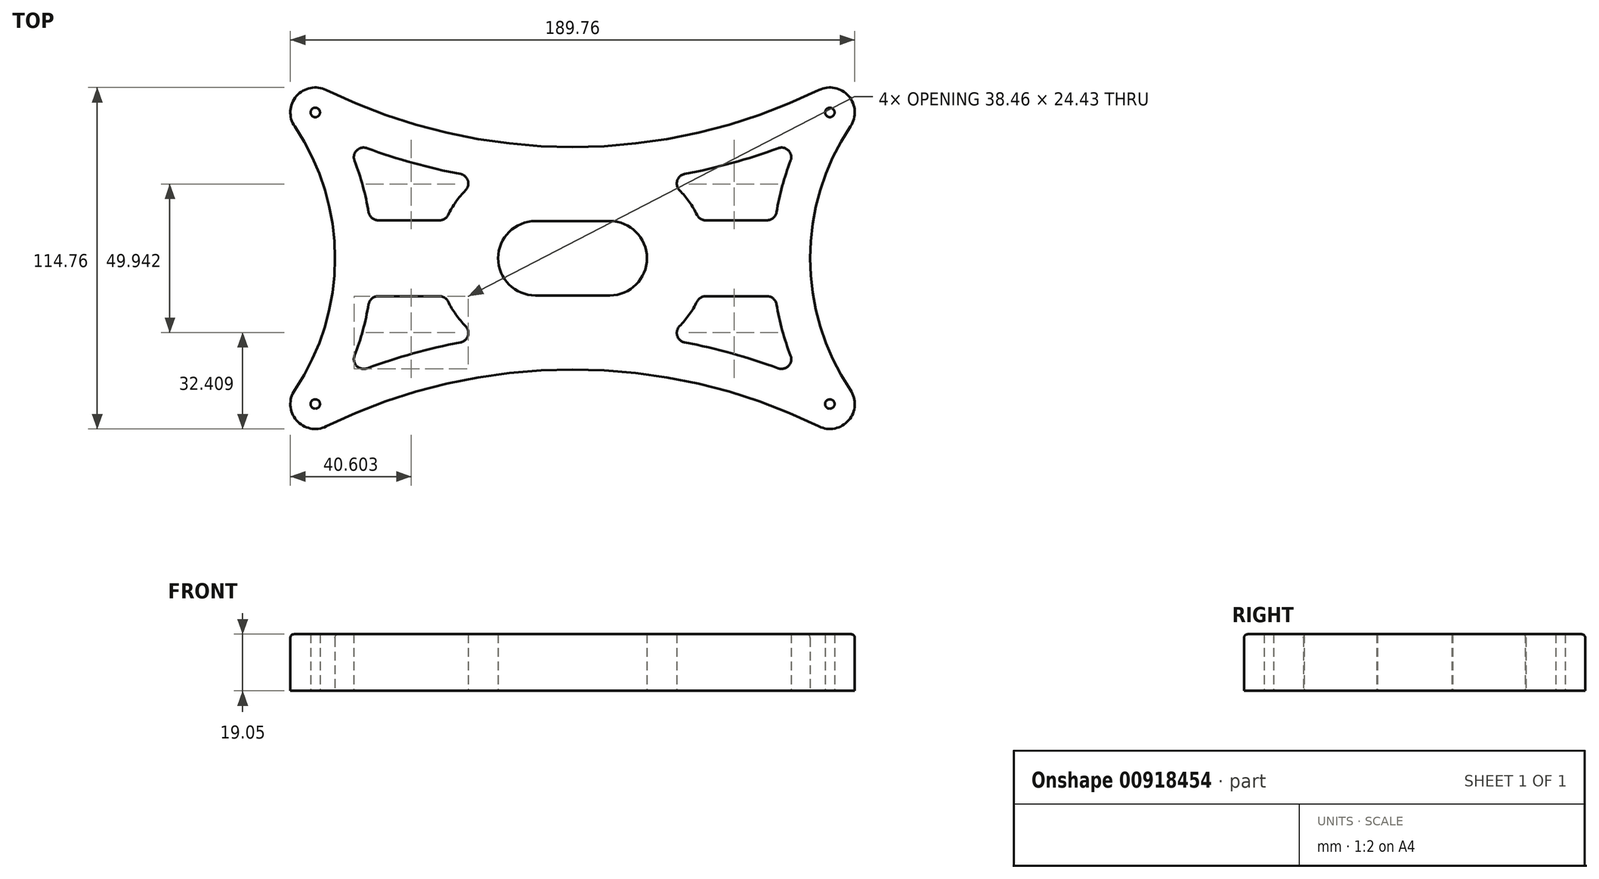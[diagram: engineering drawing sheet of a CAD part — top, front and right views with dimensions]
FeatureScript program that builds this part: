
annotation { "Feature Type Name" : "Feature", "Feature Type Description" : "" }
export const myFeature = defineFeature(function(context is Context, id is Id, definition is map)
    precondition{}
    {
        {
            var Q0;
            Q0=qCreatedBy(makeId("Top.planeOp"),FACE);
            var sketch = newSketch(context, id + "F0", { "sketchPlane" : qUnion([Q0])});
            skLineSegment(sketch, "E0.bottom", {"start": v(-102.5, 65) * mm, "end": v(102.5, 65) * mm, "construction": true});
            skLineSegment(sketch, "E0.top", {"start": v(-102.5, -65) * mm, "end": v(102.5, -65) * mm, "construction": true});
            skLineSegment(sketch, "E0.left", {"start": v(-102.5, 65) * mm, "end": v(-102.5, -65) * mm, "construction": true});
            skLineSegment(sketch, "E0.right", {"start": v(102.5, 65) * mm, "end": v(102.5, -65) * mm, "construction": true});
            skPoint(sketch, "E0.middle", {"position": v(0, 0) * mm});
            skArc(sketch, "E1", {"start": v(-79.48, 63.38) * mm, "mid": v(-98.58, 59.5) * mm, "end": v(-99.76, 40.04) * mm, "construction": true});
            skArc(sketch, "E2.MirrorC", {"start": v(79.48, 63.38) * mm, "mid": v(98.58, 59.5) * mm, "end": v(99.76, 40.04) * mm, "construction": true});
            skArc(sketch, "E3.MirrorC", {"start": v(79.48, -63.38) * mm, "mid": v(98.58, -59.5) * mm, "end": v(99.76, -40.04) * mm, "construction": true});
            skArc(sketch, "E4.MirrorC", {"start": v(-79.48, -63.38) * mm, "mid": v(-98.58, -59.5) * mm, "end": v(-99.76, -40.04) * mm, "construction": true});
            skLineSegment(sketch, "E5", {"start": v(0, 0) * mm, "end": v(0, 365.73) * mm, "construction": true});
            skPoint(sketch, "E5.endSnap0", {"position": v(0, 65) * mm});
            skLineSegment(sketch, "E6", {"start": v(0, 0) * mm, "end": v(0, -420.15) * mm, "construction": true});
            skLineSegment(sketch, "E7", {"start": v(0, 0) * mm, "end": v(397.25, 0) * mm, "construction": true});
            skPoint(sketch, "E7.endSnap0", {"position": v(102.5, 0) * mm});
            skLineSegment(sketch, "E8", {"start": v(0, 0) * mm, "end": v(-430.2, 0) * mm, "construction": true});
            skPoint(sketch, "E9", {"position": v(0, 45) * mm});
            skPoint(sketch, "E10", {"position": v(0, -45) * mm});
            skPoint(sketch, "E11", {"position": v(-87.5, 0) * mm});
            skPoint(sketch, "E12", {"position": v(87.5, 0) * mm});
            skArc(sketch, "E13", {"start": v(-79.48, 63.38) * mm, "mid": v(0, 45) * mm, "end": v(79.48, 63.38) * mm, "construction": true});
            skArc(sketch, "E14.MirrorC", {"start": v(-79.48, -63.38) * mm, "mid": v(0, -45) * mm, "end": v(79.48, -63.38) * mm, "construction": true});
            skArc(sketch, "E15", {"start": v(99.76, 40.04) * mm, "mid": v(87.5, 0) * mm, "end": v(99.76, -40.04) * mm, "construction": true});
            skArc(sketch, "E16.MirrorC", {"start": v(-99.76, 40.04) * mm, "mid": v(-87.5, 0) * mm, "end": v(-99.76, -40.04) * mm, "construction": true});
            skArc(sketch, "E17", {"start": v(-12.5, 12.5) * mm, "mid": v(-25, 0) * mm, "end": v(-12.5, -12.5) * mm});
            skArc(sketch, "E18.MirrorC", {"start": v(12.5, 12.5) * mm, "mid": v(25, 0) * mm, "end": v(12.5, -12.5) * mm});
            skLineSegment(sketch, "E19", {"start": v(-12.5, 12.5) * mm, "end": v(12.5, 12.5) * mm});
            skLineSegment(sketch, "E20", {"start": v(-12.5, -12.5) * mm, "end": v(12.5, -12.5) * mm});
            skArc(sketch, "E21.0", {"start": v(73.54, 32.7) * mm, "mid": v(70.75, 24.17) * mm, "end": v(68.8, 15.41) * mm, "construction": true});
            skArc(sketch, "E21.1", {"start": v(-69.07, 37.24) * mm, "mid": v(-53.53, 32.26) * mm, "end": v(-37.64, 28.55) * mm, "construction": true});
            skArc(sketch, "E21.2", {"start": v(-73.54, 32.7) * mm, "mid": v(-70.75, 24.17) * mm, "end": v(-68.8, 15.41) * mm, "construction": true});
            skArc(sketch, "E21.3", {"start": v(-69.07, -37.24) * mm, "mid": v(-53.53, -32.26) * mm, "end": v(-37.64, -28.55) * mm, "construction": true});
            skArc(sketch, "E22.0", {"start": v(-35.78, 22.67) * mm, "mid": v(-39.02, 18.79) * mm, "end": v(-41.61, 14.44) * mm, "construction": true});
            skArc(sketch, "E22.2", {"start": v(35.78, 22.67) * mm, "mid": v(39.02, 18.79) * mm, "end": v(41.61, 14.44) * mm, "construction": true});
            skPoint(sketch, "E23.visualSharp", {"position": v(-76.83, 40.26) * mm});
            skArc(sketch, "E23.filletArc", {"start": v(-69.07, 37.24) * mm, "mid": v(-72.76, 36.4) * mm, "end": v(-73.54, 32.7) * mm, "construction": true});
            skLineSegment(sketch, "E24", {"start": v(-44.75, 12.5) * mm, "end": v(-65.36, 12.5) * mm, "construction": true});
            skLineSegment(sketch, "E25", {"start": v(-44.75, -12.5) * mm, "end": v(-65.36, -12.5) * mm, "construction": true});
            skLineSegment(sketch, "E26", {"start": v(44.75, 12.5) * mm, "end": v(65.36, 12.5) * mm, "construction": true});
            skLineSegment(sketch, "E27", {"start": v(44.75, -12.5) * mm, "end": v(65.36, -12.5) * mm, "construction": true});
            skArc(sketch, "E28.trimOffspring", {"start": v(41.61, -14.44) * mm, "mid": v(39.02, -18.79) * mm, "end": v(35.78, -22.67) * mm, "construction": true});
            skArc(sketch, "E29.trimOffspring", {"start": v(68.8, -15.41) * mm, "mid": v(70.75, -24.17) * mm, "end": v(73.54, -32.7) * mm, "construction": true});
            skArc(sketch, "E30.trimOffspring", {"start": v(37.64, 28.55) * mm, "mid": v(53.53, 32.26) * mm, "end": v(69.07, 37.24) * mm, "construction": true});
            skArc(sketch, "E31.trimOffspring", {"start": v(37.64, -28.55) * mm, "mid": v(53.53, -32.26) * mm, "end": v(69.07, -37.24) * mm, "construction": true});
            skArc(sketch, "E32.trimOffspring", {"start": v(-41.61, -14.44) * mm, "mid": v(-39.02, -18.79) * mm, "end": v(-35.78, -22.67) * mm, "construction": true});
            skArc(sketch, "E33.trimOffspring", {"start": v(-68.8, -15.41) * mm, "mid": v(-70.75, -24.17) * mm, "end": v(-73.54, -32.7) * mm, "construction": true});
            skPoint(sketch, "E34.visualSharp", {"position": v(-30.17, 27.28) * mm});
            skArc(sketch, "E34.filletArc", {"start": v(-35.78, 22.67) * mm, "mid": v(-34.95, 26.17) * mm, "end": v(-37.64, 28.55) * mm, "construction": true});
            skPoint(sketch, "E35.visualSharp", {"position": v(-42.5, 12.5) * mm});
            skArc(sketch, "E35.filletArc", {"start": v(-44.75, 12.5) * mm, "mid": v(-42.9, 13.03) * mm, "end": v(-41.61, 14.44) * mm, "construction": true});
            skPoint(sketch, "E36.visualSharp", {"position": v(-68.36, 12.5) * mm});
            skArc(sketch, "E36.filletArc", {"start": v(-68.8, 15.41) * mm, "mid": v(-67.61, 13.32) * mm, "end": v(-65.36, 12.5) * mm, "construction": true});
            skPoint(sketch, "E37.visualSharp", {"position": v(-68.36, -12.5) * mm});
            skArc(sketch, "E37.filletArc", {"start": v(-65.36, -12.5) * mm, "mid": v(-67.61, -13.32) * mm, "end": v(-68.8, -15.41) * mm, "construction": true});
            skPoint(sketch, "E38.visualSharp", {"position": v(-42.5, -12.5) * mm});
            skArc(sketch, "E38.filletArc", {"start": v(-41.61, -14.44) * mm, "mid": v(-42.9, -13.03) * mm, "end": v(-44.75, -12.5) * mm, "construction": true});
            skPoint(sketch, "E39.visualSharp", {"position": v(-30.17, -27.28) * mm});
            skArc(sketch, "E39.filletArc", {"start": v(-37.64, -28.55) * mm, "mid": v(-34.95, -26.17) * mm, "end": v(-35.78, -22.67) * mm, "construction": true});
            skPoint(sketch, "E40.visualSharp", {"position": v(-76.83, -40.26) * mm});
            skArc(sketch, "E40.filletArc", {"start": v(-73.54, -32.7) * mm, "mid": v(-72.76, -36.4) * mm, "end": v(-69.07, -37.24) * mm, "construction": true});
            skPoint(sketch, "E41.visualSharp", {"position": v(30.17, 27.28) * mm});
            skArc(sketch, "E41.filletArc", {"start": v(37.64, 28.55) * mm, "mid": v(34.95, 26.17) * mm, "end": v(35.78, 22.67) * mm, "construction": true});
            skPoint(sketch, "E42.visualSharp", {"position": v(76.83, 40.26) * mm});
            skArc(sketch, "E42.filletArc", {"start": v(73.54, 32.7) * mm, "mid": v(72.76, 36.4) * mm, "end": v(69.07, 37.24) * mm, "construction": true});
            skPoint(sketch, "E43.visualSharp", {"position": v(68.36, 12.5) * mm});
            skArc(sketch, "E43.filletArc", {"start": v(65.36, 12.5) * mm, "mid": v(67.61, 13.32) * mm, "end": v(68.8, 15.41) * mm, "construction": true});
            skPoint(sketch, "E44.visualSharp", {"position": v(42.5, 12.5) * mm});
            skArc(sketch, "E44.filletArc", {"start": v(41.61, 14.44) * mm, "mid": v(42.9, 13.03) * mm, "end": v(44.75, 12.5) * mm, "construction": true});
            skPoint(sketch, "E45.visualSharp", {"position": v(42.5, -12.5) * mm});
            skArc(sketch, "E45.filletArc", {"start": v(44.75, -12.5) * mm, "mid": v(42.9, -13.03) * mm, "end": v(41.61, -14.44) * mm, "construction": true});
            skPoint(sketch, "E46.visualSharp", {"position": v(68.36, -12.5) * mm});
            skArc(sketch, "E46.filletArc", {"start": v(68.8, -15.41) * mm, "mid": v(67.61, -13.32) * mm, "end": v(65.36, -12.5) * mm, "construction": true});
            skPoint(sketch, "E47.visualSharp", {"position": v(76.83, -40.26) * mm});
            skArc(sketch, "E47.filletArc", {"start": v(69.07, -37.24) * mm, "mid": v(72.76, -36.4) * mm, "end": v(73.54, -32.7) * mm, "construction": true});
            skPoint(sketch, "E48.visualSharp", {"position": v(30.17, -27.28) * mm});
            skArc(sketch, "E48.filletArc", {"start": v(35.78, -22.67) * mm, "mid": v(34.95, -26.17) * mm, "end": v(37.64, -28.55) * mm, "construction": true});
            skCircle(sketch, "E49", {"center": v(-12.5, 0) * mm, "radius": 3.18 * mm});
            skCircle(sketch, "E50", {"center": v(12.5, 0) * mm, "radius": 3.18 * mm});
            skArc(sketch, "E51.0", {"start": v(-82.82, 56.53) * mm, "mid": v(-92.82, 54.5) * mm, "end": v(-93.44, 44.3) * mm});
            skArc(sketch, "E51.1", {"start": v(-93.44, 44.3) * mm, "mid": v(-79.88, 0) * mm, "end": v(-93.44, -44.3) * mm});
            skArc(sketch, "E51.2", {"start": v(-82.82, 56.53) * mm, "mid": v(0, 37.38) * mm, "end": v(82.82, 56.53) * mm});
            skArc(sketch, "E51.3", {"start": v(-82.82, -56.53) * mm, "mid": v(-92.82, -54.5) * mm, "end": v(-93.44, -44.3) * mm});
            skArc(sketch, "E51.4", {"start": v(82.82, 56.53) * mm, "mid": v(92.82, 54.5) * mm, "end": v(93.44, 44.3) * mm});
            skArc(sketch, "E51.5", {"start": v(93.44, 44.3) * mm, "mid": v(79.88, 0) * mm, "end": v(93.44, -44.3) * mm});
            skArc(sketch, "E51.6", {"start": v(82.82, -56.53) * mm, "mid": v(92.82, -54.5) * mm, "end": v(93.44, -44.3) * mm});
            skArc(sketch, "E51.7", {"start": v(-82.82, -56.53) * mm, "mid": v(0, -37.38) * mm, "end": v(82.82, -56.53) * mm});
            skCircle(sketch, "E52", {"center": v(-86.5, -49) * mm, "radius": 1.59 * mm});
            skCircle(sketch, "E53", {"center": v(86.5, -49) * mm, "radius": 1.59 * mm});
            skCircle(sketch, "E54", {"center": v(86.5, 49) * mm, "radius": 1.59 * mm});
            skCircle(sketch, "E55", {"center": v(-86.5, 49) * mm, "radius": 1.59 * mm});
            skArc(sketch, "E56.0", {"start": v(-41.84, -14.56) * mm, "mid": v(-43.04, -13.24) * mm, "end": v(-44.75, -12.75) * mm});
            skArc(sketch, "E56.1", {"start": v(-41.84, -14.56) * mm, "mid": v(-39.23, -18.93) * mm, "end": v(-35.97, -22.85) * mm});
            skLineSegment(sketch, "E56.2", {"start": v(-44.75, -12.75) * mm, "end": v(-65.36, -12.75) * mm});
            skArc(sketch, "E56.3", {"start": v(-37.68, -28.3) * mm, "mid": v(-35.2, -26.1) * mm, "end": v(-35.97, -22.85) * mm});
            skArc(sketch, "E56.4", {"start": v(-65.36, -12.75) * mm, "mid": v(-67.45, -13.52) * mm, "end": v(-68.56, -15.45) * mm});
            skArc(sketch, "E56.5", {"start": v(-68.56, -15.45) * mm, "mid": v(-70.5, -24.24) * mm, "end": v(-73.3, -32.79) * mm});
            skArc(sketch, "E56.6", {"start": v(-73.3, -32.79) * mm, "mid": v(-72.58, -36.23) * mm, "end": v(-69.16, -37) * mm});
            skArc(sketch, "E56.7", {"start": v(-69.16, -37) * mm, "mid": v(-53.6, -32.01) * mm, "end": v(-37.68, -28.3) * mm});
            skLineSegment(sketch, "E57.0", {"start": v(-12.5, 12.25) * mm, "end": v(12.5, 12.25) * mm, "construction": true});
            skArc(sketch, "E57.1", {"start": v(-12.5, 12.25) * mm, "mid": v(-24.75, 0) * mm, "end": v(-12.5, -12.25) * mm, "construction": true});
            skLineSegment(sketch, "E57.2", {"start": v(-12.5, -12.25) * mm, "end": v(12.5, -12.25) * mm, "construction": true});
            skArc(sketch, "E57.3", {"start": v(12.5, 12.25) * mm, "mid": v(24.75, 0) * mm, "end": v(12.5, -12.25) * mm, "construction": true});
            skArc(sketch, "E58.0", {"start": v(68.56, -15.45) * mm, "mid": v(67.45, -13.52) * mm, "end": v(65.36, -12.75) * mm});
            skLineSegment(sketch, "E58.1", {"start": v(44.75, -12.75) * mm, "end": v(65.36, -12.75) * mm});
            skArc(sketch, "E58.2", {"start": v(68.56, -15.45) * mm, "mid": v(70.5, -24.24) * mm, "end": v(73.3, -32.79) * mm});
            skArc(sketch, "E58.3", {"start": v(44.75, -12.75) * mm, "mid": v(43.04, -13.24) * mm, "end": v(41.84, -14.56) * mm});
            skArc(sketch, "E58.4", {"start": v(69.16, -37) * mm, "mid": v(72.58, -36.23) * mm, "end": v(73.3, -32.79) * mm});
            skArc(sketch, "E58.5", {"start": v(37.68, -28.3) * mm, "mid": v(53.6, -32.01) * mm, "end": v(69.16, -37) * mm});
            skArc(sketch, "E58.6", {"start": v(35.97, -22.85) * mm, "mid": v(35.2, -26.1) * mm, "end": v(37.68, -28.3) * mm});
            skArc(sketch, "E58.7", {"start": v(41.84, -14.56) * mm, "mid": v(39.23, -18.93) * mm, "end": v(35.97, -22.85) * mm});
            skArc(sketch, "E59.0", {"start": v(37.68, 28.3) * mm, "mid": v(35.2, 26.1) * mm, "end": v(35.97, 22.85) * mm});
            skArc(sketch, "E59.1", {"start": v(35.97, 22.85) * mm, "mid": v(39.23, 18.93) * mm, "end": v(41.84, 14.56) * mm});
            skArc(sketch, "E59.2", {"start": v(37.68, 28.3) * mm, "mid": v(53.6, 32.01) * mm, "end": v(69.16, 37) * mm});
            skArc(sketch, "E59.3", {"start": v(41.84, 14.56) * mm, "mid": v(43.04, 13.24) * mm, "end": v(44.75, 12.75) * mm});
            skArc(sketch, "E59.4", {"start": v(73.3, 32.79) * mm, "mid": v(72.58, 36.23) * mm, "end": v(69.16, 37) * mm});
            skArc(sketch, "E59.5", {"start": v(73.3, 32.79) * mm, "mid": v(70.5, 24.24) * mm, "end": v(68.56, 15.45) * mm});
            skArc(sketch, "E59.6", {"start": v(65.36, 12.75) * mm, "mid": v(67.45, 13.52) * mm, "end": v(68.56, 15.45) * mm});
            skLineSegment(sketch, "E59.7", {"start": v(44.75, 12.75) * mm, "end": v(65.36, 12.75) * mm});
            skArc(sketch, "E60.0", {"start": v(-69.16, 37) * mm, "mid": v(-72.58, 36.23) * mm, "end": v(-73.3, 32.79) * mm});
            skArc(sketch, "E60.1", {"start": v(-73.3, 32.79) * mm, "mid": v(-70.5, 24.24) * mm, "end": v(-68.56, 15.45) * mm});
            skArc(sketch, "E60.2", {"start": v(-69.16, 37) * mm, "mid": v(-53.6, 32.01) * mm, "end": v(-37.68, 28.3) * mm});
            skArc(sketch, "E60.3", {"start": v(-68.56, 15.45) * mm, "mid": v(-67.45, 13.52) * mm, "end": v(-65.36, 12.75) * mm});
            skArc(sketch, "E60.4", {"start": v(-35.97, 22.85) * mm, "mid": v(-35.2, 26.1) * mm, "end": v(-37.68, 28.3) * mm});
            skArc(sketch, "E60.5", {"start": v(-35.97, 22.85) * mm, "mid": v(-39.23, 18.93) * mm, "end": v(-41.84, 14.56) * mm});
            skArc(sketch, "E60.6", {"start": v(-44.75, 12.75) * mm, "mid": v(-43.04, 13.24) * mm, "end": v(-41.84, 14.56) * mm});
            skLineSegment(sketch, "E60.7", {"start": v(-44.75, 12.75) * mm, "end": v(-65.36, 12.75) * mm});
            skSolve(sketch);
        }
        {
            var Q0;
            Q0=makeQuery(id+"F0.imprint","IMPRINT",FACE,{"disambiguationData":[TD([[makeQuery(id+"F0.imprint","IMPRINT",EDGE,{"derivedFrom":sQuery(id+"F0.wireOp",EDGE,"E51.0")}),1.0]])]});
            extrude(context, id + "F1", {"entities" : qUnion([Q0]), "depth" : 19.05 * mm, "offsetDistance" : 25.4 * mm});
        }
        {
            var Q0;
            Q0=makeQuery(id+"F0.imprint","IMPRINT",FACE,{"disambiguationData":[TD([[makeQuery(id+"F0.imprint","IMPRINT",EDGE,{"derivedFrom":sQuery(id+"F0.wireOp",EDGE,"E49")}),-1.0]])]});
            var Q1;
            Q1=makeQuery(id+"F0.imprint","IMPRINT",FACE,{"disambiguationData":[TD([[makeQuery(id+"F0.imprint","IMPRINT",EDGE,{"derivedFrom":sQuery(id+"F0.wireOp",EDGE,"E50")}),-1.0]])]});
            extrude(context, id + "F2", {"entities" : qUnion([Q0, Q1]), "operationType" : NewBodyOperationType.REMOVE, "depth" : 6.35 * mm, "offsetDistance" : 25.4 * mm});
        }
        {
            var Q0;
            Q0=makeQuery(id+"F1.opExtrude","CAP_EDGE",EDGE,{"disambiguationData":[OSD([sQuery(id+"F0.wireOp",EDGE,"E51.1")])],"isStart":false});
            var Q1;
            Q1=makeQuery(id+"F1.opExtrude","CAP_EDGE",EDGE,{"disambiguationData":[OSD([sQuery(id+"F0.wireOp",EDGE,"E51.3")])],"isStart":false});
            var Q2;
            Q2=makeQuery(id+"F1.opExtrude","CAP_EDGE",EDGE,{"disambiguationData":[OSD([sQuery(id+"F0.wireOp",EDGE,"E51.7")])],"isStart":false});
            var Q3;
            Q3=makeQuery(id+"F1.opExtrude","CAP_EDGE",EDGE,{"disambiguationData":[OSD([sQuery(id+"F0.wireOp",EDGE,"E51.6")])],"isStart":false});
            var Q4;
            Q4=makeQuery(id+"F1.opExtrude","CAP_EDGE",EDGE,{"disambiguationData":[OSD([sQuery(id+"F0.wireOp",EDGE,"E51.5")])],"isStart":false});
            var Q5;
            Q5=makeQuery(id+"F1.opExtrude","CAP_EDGE",EDGE,{"disambiguationData":[OSD([sQuery(id+"F0.wireOp",EDGE,"E51.4")])],"isStart":false});
            var Q6;
            Q6=makeQuery(id+"F1.opExtrude","CAP_EDGE",EDGE,{"disambiguationData":[OSD([sQuery(id+"F0.wireOp",EDGE,"E51.2")])],"isStart":false});
            var Q7;
            Q7=makeQuery(id+"F1.opExtrude","CAP_EDGE",EDGE,{"disambiguationData":[OSD([sQuery(id+"F0.wireOp",EDGE,"E51.0")])],"isStart":false});
            var Q8;
            Q8=makeQuery(id+"FaSwRgSjZTw18kr_0.opExtrude","CAP_EDGE",EDGE,{"disambiguationData":[OSD([sQuery(id+"F0.wireOp",EDGE,"E57.3")])],"isStart":false});
            fillet(context, id + "F3", {"entities" : qUnion([Q0, Q1, Q2, Q3, Q4, Q5, Q6, Q7, Q8]), "radius" : 1.27 * mm, "tangentPropagation" : true, "allowEdgeOverflow" : false});
        }
    });
